# Revit family: FU_Modular_Plania Config 3
name_source: partatom
category: Furniture
units: mm (PartAtom-declared; Revit-internal decimal feet)

## family parameters
Always vertical = Yes
Cut with Voids When Loaded = No
OmniClass Number = 23.40.20.00
OmniClass Title = General Furniture and Specialties
Room Calculation Point = No
Shared = No
Work Plane-Based = No

## types (1)
- Plania Bench Configuration 3
    Default Elevation = 0 mm  [stored 0 ft]
    Description = More than a simple bench, PLANIA is a complete system of modular benches that are available, with or without backrest, in various sizes and with different types of legs. The pictured configuration uses four benches without a backrest and one connecting central table in oak. Please contact one of our representatives to discover all Plania’s possible configurations.
    Manufacturer = Sandler
    Model = Plania
    URL = https://www.sandlerseating.com

note: [stored X ft] marks values corroborated as IEEE doubles in the binary element streams (Revit-internal decimal feet)

## geometry (parser evidence)
native form markers: Sweep x9
no freeform markers — native parametric forms only
